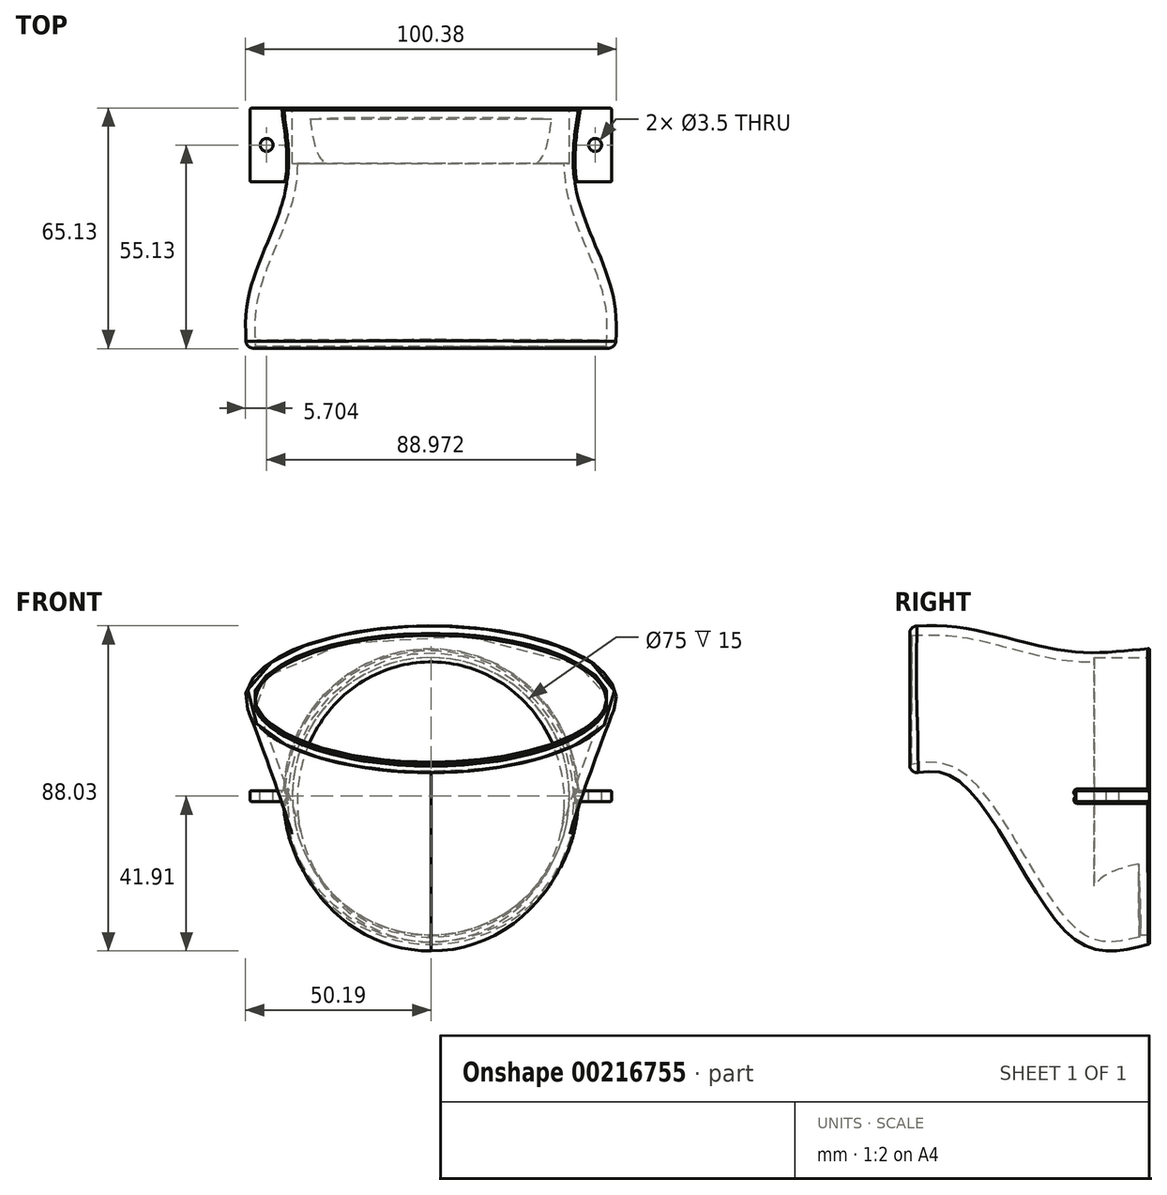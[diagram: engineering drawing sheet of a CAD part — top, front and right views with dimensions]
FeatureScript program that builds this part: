
annotation { "Feature Type Name" : "Feature", "Feature Type Description" : "" }
export const myFeature = defineFeature(function(context is Context, id is Id, definition is map)
    precondition{}
    {
        {
            var Q0;
            Q0=qCreatedBy(makeId("Front.planeOp"),FACE);
            var sketch = newSketch(context, id + "F0", { "sketchPlane" : qUnion([Q0])});
            skCircle(sketch, "E0", {"center": v(0, 0) * mm, "radius": 40 * mm});
            skSolve(sketch);
        }
        {
            var Q0;
            Q0=qCreatedBy(makeId("Front.planeOp"),FACE);
            cPlane(context, id + "F1", {"entities" : qUnion([Q0]), "cplaneType" : CPlaneType.OFFSET, "offset" : 20 * mm, "width" : 150 * mm, "height" : 150 * mm});
        }
        {
            var Q0;
            Q0=qCreatedBy(id+"F1.planeOp",FACE);
            var sketch = newSketch(context, id + "F2", { "sketchPlane" : qUnion([Q0])});
            skCircle(sketch, "E1", {"center": v(0, 0) * mm, "radius": 39 * mm});
            skSolve(sketch);
        }
        {
            var Q0;
            Q0=qCreatedBy(id+"F1.planeOp",FACE);
            cPlane(context, id + "F3", {"entities" : qUnion([Q0]), "cplaneType" : CPlaneType.OFFSET, "offset" : 35 * mm, "width" : 150 * mm, "height" : 150 * mm});
        }
        {
            var Q0;
            Q0=qCreatedBy(id+"F3.planeOp",FACE);
            var sketch = newSketch(context, id + "F4", { "sketchPlane" : qUnion([Q0])});
            skEllipse(sketch, "E2", {"center": v(0, 26) * mm, "majorRadius": 50 * mm, "minorRadius": 20 * mm, "majorAxis": v(1, 0)});
            skSolve(sketch);
        }
        {
            var Q0;
            Q0=qCreatedBy(id+"F3.planeOp",FACE);
            cPlane(context, id + "F5", {"entities" : qUnion([Q0]), "cplaneType" : CPlaneType.OFFSET, "offset" : 10 * mm, "width" : 150 * mm, "height" : 150 * mm});
        }
        {
            var Q0;
            Q0=qCreatedBy(id+"F5.planeOp",FACE);
            var sketch = newSketch(context, id + "F6", { "sketchPlane" : qUnion([Q0])});
            skEllipse(sketch, "E3", {"center": v(0, 26) * mm, "majorRadius": 50 * mm, "minorRadius": 20 * mm, "majorAxis": v(1, 0)});
            skSolve(sketch);
        }
        {
            var Q0;
            Q0=makeQuery(id+"F0.imprint","IMPRINT",FACE,{"disambiguationData":[TD([[makeQuery(id+"F0.imprint","IMPRINT",EDGE,{"derivedFrom":sQuery(id+"F0.wireOp",EDGE,"E0")}),1.0]])]});
            var Q1;
            Q1=makeQuery(id+"F2.imprint","IMPRINT",FACE,{"disambiguationData":[TD([[makeQuery(id+"F2.imprint","IMPRINT",EDGE,{"derivedFrom":sQuery(id+"F2.wireOp",EDGE,"E1")}),1.0]])]});
            var Q2;
            Q2=makeQuery(id+"F4.imprint","IMPRINT",FACE,{"disambiguationData":[TD([[makeQuery(id+"F4.imprint","IMPRINT",EDGE,{"derivedFrom":sQuery(id+"F4.wireOp",EDGE,"E2")}),1.0]])]});
            var Q3;
            Q3=makeQuery(id+"F6.imprint","IMPRINT",FACE,{"disambiguationData":[TD([[makeQuery(id+"F6.imprint","IMPRINT",EDGE,{"derivedFrom":sQuery(id+"F6.wireOp",EDGE,"E3")}),1.0]])]});
            loft(context, id + "F7", {"sheetProfilesArray" : [{ "sheetProfileEntities" : qUnion([Q0]) }, { "sheetProfileEntities" : qUnion([Q1]) }, { "sheetProfileEntities" : qUnion([Q2]) }, { "sheetProfileEntities" : qUnion([Q3]) }]});
        }
        {
            var Q0;
            Q0=qCreatedBy(makeId("Right.planeOp"),FACE);
            cPlane(context, id + "F8", {"entities" : qUnion([Q0]), "cplaneType" : CPlaneType.OFFSET, "offset" : 49 * mm, "width" : 150 * mm, "height" : 150 * mm});
        }
        {
            var Q0;
            Q0=qCreatedBy(id+"F8.planeOp",FACE);
            var sketch = newSketch(context, id + "F9", { "sketchPlane" : qUnion([Q0])});
            skLineSegment(sketch, "E4.bottom", {"start": v(-20, 1.5) * mm, "end": v(0, 1.5) * mm});
            skLineSegment(sketch, "E4.top", {"start": v(-20, -1.5) * mm, "end": v(0, -1.5) * mm});
            skLineSegment(sketch, "E4.left", {"start": v(-20, 1.5) * mm, "end": v(-20, -1.5) * mm});
            skLineSegment(sketch, "E4.right", {"start": v(0, 1.5) * mm, "end": v(0, -1.5) * mm});
            skSolve(sketch);
        }
        {
            var Q0;
            Q0=makeQuery(id+"F7.opLoft","CAP_FACE",FACE,{"disambiguationData":[OSD([makeQuery(id+"F6.imprint","IMPRINT",FACE,{"disambiguationData":[TD([[makeQuery(id+"F6.imprint","IMPRINT",EDGE,{"derivedFrom":sQuery(id+"F6.wireOp",EDGE,"E3")}),1.0]])]})])],"isStart":true});
            var Q1;
            Q1=makeQuery(id+"F7.opLoft","SWEPT_BODY",BODY,{"disambiguationData":[OSD([makeQuery(id+"F0.imprint","IMPRINT",FACE,{"disambiguationData":[TD([[makeQuery(id+"F0.imprint","IMPRINT",EDGE,{"derivedFrom":sQuery(id+"F0.wireOp",EDGE,"E0")}),1.0]])]}),sQuery(id+"F2.wireOp",EDGE,"E1"),sQuery(id+"F4.wireOp",EDGE,"E2"),makeQuery(id+"F6.imprint","IMPRINT",FACE,{"disambiguationData":[TD([[makeQuery(id+"F6.imprint","IMPRINT",EDGE,{"derivedFrom":sQuery(id+"F6.wireOp",EDGE,"E3")}),1.0]])]})])]});
            shell(context, id + "F10", {"entities" : qUnion([Q0]), "parts" : qUnion([Q1]), "thickness" : 2.5 * mm});
        }
        {
            var Q0;
            Q0=makeQuery(id+"F7.opLoft","CAP_FACE",FACE,{"disambiguationData":[OSD([makeQuery(id+"F0.imprint","IMPRINT",FACE,{"disambiguationData":[TD([[makeQuery(id+"F0.imprint","IMPRINT",EDGE,{"derivedFrom":sQuery(id+"F0.wireOp",EDGE,"E0")}),1.0]])]})])],"isStart":true});
            var sketch = newSketch(context, id + "F11", { "sketchPlane" : qUnion([Q0])});
            skCircle(sketch, "E5", {"center": v(0, 0) * mm, "radius": 37.5 * mm});
            skSolve(sketch);
        }
        {
            var Q0;
            Q0 = qSketchRegion(id + "F11", true);
            extrude(context, id + "F12", {"entities" : qUnion([Q0]), "operationType" : NewBodyOperationType.REMOVE, "oppositeDirection" : true, "depth" : 15 * mm});
        }
        {
            var Q0;
            Q0 = qSketchRegion(id + "F9", true);
            extrude(context, id + "F13", {"entities" : qUnion([Q0]), "operationType" : NewBodyOperationType.ADD, "oppositeDirection" : true, "depth" : 11 * mm});
        }
        {
            var Q0;
            Q0=qCreatedBy(makeId("Right.planeOp"),FACE);
            cPlane(context, id + "F14", {"entities" : qUnion([Q0]), "cplaneType" : CPlaneType.OFFSET, "offset" : 49 * mm, "oppositeDirection" : true, "width" : 150 * mm, "height" : 150 * mm});
        }
        {
            var Q0;
            Q0=qCreatedBy(id+"F14.planeOp",FACE);
            var sketch = newSketch(context, id + "F15", { "sketchPlane" : qUnion([Q0])});
            skLineSegment(sketch, "E6.bottom", {"start": v(0, 1.5) * mm, "end": v(-20, 1.5) * mm});
            skLineSegment(sketch, "E6.top", {"start": v(0, -1.5) * mm, "end": v(-20, -1.5) * mm});
            skLineSegment(sketch, "E6.left", {"start": v(0, 1.5) * mm, "end": v(0, -1.5) * mm});
            skLineSegment(sketch, "E6.right", {"start": v(-20, 1.5) * mm, "end": v(-20, -1.5) * mm});
            skSolve(sketch);
        }
        {
            var Q0;
            Q0 = qSketchRegion(id + "F15", true);
            var Q1;
            Q1 = qSketchRegion(id + "F17", true);
            extrude(context, id + "F16", {"entities" : qUnion([Q0, Q1]), "operationType" : NewBodyOperationType.ADD, "depth" : 11 * mm});
        }
        {
            var Q0;
            Q0=makeQuery(id+"F16.opExtrude","SWEPT_FACE",FACE,{"disambiguationData":[OSD([sQuery(id+"F15.wireOp",EDGE,"E6.bottom")])]});
            var sketch = newSketch(context, id + "F17", { "sketchPlane" : qUnion([Q0])});
            skCircle(sketch, "E7", {"center": v(-44.49, -10) * mm, "radius": 1.75 * mm});
            skPoint(sketch, "E7.centerSnap0", {"position": v(-44.49, 0) * mm});
            skCircle(sketch, "E8.MirrorC", {"center": v(44.49, -10) * mm, "radius": 1.75 * mm});
            skSolve(sketch);
        }
        {
            var Q0;
            Q0 = qSketchRegion(id + "F17", true);
            extrude(context, id + "F18", {"entities" : qUnion([Q0]), "operationType" : NewBodyOperationType.REMOVE, "endBound" : BoundingType.THROUGH_ALL, "oppositeDirection" : true, "depth" : 25 * mm});
        }
        {
            var Q0;
            Q0=makeQuery(id+"F12.boolean.opBoolean","COPY",EDGE,{"derivedFrom":makeQuery(id+"F12.opExtrude","CAP_EDGE",EDGE,{"disambiguationData":[OSD([sQuery(id+"F11.wireOp",EDGE,"E5")])],"isStart":true})});
            var Q1;
            Q1=makeQuery(id+"F10.opShell","OFFSET_EDGE",EDGE,{"disambiguationData":[OSD([sQuery(id+"F0.wireOp",EDGE,"E0"),sQuery(id+"F6.wireOp",EDGE,"E3")])]});
            chamfer(context, id + "F19", {"entities" : qUnion([Q0, Q1]), "width" : .5 * mm, "tangentPropagation" : true});
        }
        {
            var Q0;
            Q0=makeQuery(id+"F7.opLoft","MID_CAP_EDGE",EDGE,{"disambiguationData":[OSD([sQuery(id+"F0.wireOp",EDGE,"E0"),sQuery(id+"F6.wireOp",EDGE,"E3")])],"capPos":3.0});
            fillet(context, id + "F20", {"entities" : qUnion([Q0]), "radius" : 2 * mm, "tangentPropagation" : true, "allowEdgeOverflow" : false});
        }
        {
            var Q0;
            Q0=makeQuery(id+"F13.boolean.opBoolean","INTERSECT",EDGE,{"derivedFrom":[makeQuery(id+"F7.opLoft","SWEPT_FACE",FACE,{"disambiguationData":[OSD([sQuery(id+"F0.wireOp",EDGE,"E0"),sQuery(id+"F2.wireOp",EDGE,"E1")])]}),makeQuery(id+"F13.opExtrude","SWEPT_FACE",FACE,{"disambiguationData":[OSD([sQuery(id+"F9.wireOp",EDGE,"E4.bottom")])]})]});
            var Q1;
            Q1=makeQuery(id+"F13.boolean.opBoolean","INTERSECT",EDGE,{"derivedFrom":[makeQuery(id+"F7.opLoft","SWEPT_FACE",FACE,{"disambiguationData":[OSD([sQuery(id+"F0.wireOp",EDGE,"E0"),sQuery(id+"F2.wireOp",EDGE,"E1")])]}),makeQuery(id+"F13.opExtrude","SWEPT_FACE",FACE,{"disambiguationData":[OSD([sQuery(id+"F9.wireOp",EDGE,"E4.top")])]})]});
            var Q2;
            {var subQ0=sQuery(id+"F0.wireOp",EDGE,"E0");Q2=makeQuery(id+"F16.boolean.opBoolean","SPLIT",EDGE,{"disambiguationData":[TD([makeQuery(id+"F13.opExtrude","SWEPT_FACE",FACE,{"disambiguationData":[OSD([sQuery(id+"F9.wireOp",EDGE,"E4.bottom")])]})])],"derivedFrom":makeQuery(id+"F7.opLoft","MID_CAP_EDGE",EDGE,{"disambiguationData":[OSD([subQ0])],"capPos":0.0})});}
            var Q3;
            {var subQ0=sQuery(id+"F0.wireOp",EDGE,"E0");Q3=makeQuery(id+"F16.boolean.opBoolean","SPLIT",EDGE,{"disambiguationData":[TD([makeQuery(id+"F13.opExtrude","SWEPT_FACE",FACE,{"disambiguationData":[OSD([sQuery(id+"F9.wireOp",EDGE,"E4.top")])]})])],"derivedFrom":makeQuery(id+"F7.opLoft","MID_CAP_EDGE",EDGE,{"disambiguationData":[OSD([subQ0])],"capPos":0.0})});}
            var Q4;
            Q4=makeQuery(id+"F16.opExtrude","SWEPT_EDGE",EDGE,{"disambiguationData":[OSD([sQuery(id+"F15.wireOp",EDGE,"E6.bottom"),sQuery(id+"F15.wireOp",EDGE,"E6.left")])]});
            var Q5;
            Q5=makeQuery(id+"F16.opExtrude","SWEPT_EDGE",EDGE,{"disambiguationData":[OSD([sQuery(id+"F15.wireOp",EDGE,"E6.top"),sQuery(id+"F15.wireOp",EDGE,"E6.left")])]});
            var Q6;
            Q6=makeQuery(id+"F16.boolean.opBoolean","INTERSECT",EDGE,{"derivedFrom":[makeQuery(id+"F7.opLoft","SWEPT_FACE",FACE,{"disambiguationData":[OSD([sQuery(id+"F0.wireOp",EDGE,"E0"),sQuery(id+"F2.wireOp",EDGE,"E1")])]}),makeQuery(id+"F16.opExtrude","SWEPT_FACE",FACE,{"disambiguationData":[OSD([sQuery(id+"F15.wireOp",EDGE,"E6.bottom")])]})]});
            var Q7;
            Q7=makeQuery(id+"F16.boolean.opBoolean","INTERSECT",EDGE,{"derivedFrom":[makeQuery(id+"F7.opLoft","SWEPT_FACE",FACE,{"disambiguationData":[OSD([sQuery(id+"F0.wireOp",EDGE,"E0"),sQuery(id+"F2.wireOp",EDGE,"E1")])]}),makeQuery(id+"F16.opExtrude","SWEPT_FACE",FACE,{"disambiguationData":[OSD([sQuery(id+"F15.wireOp",EDGE,"E6.top")])]})]});
            var Q8;
            Q8=makeQuery(id+"F16.opExtrude","SWEPT_EDGE",EDGE,{"disambiguationData":[OSD([sQuery(id+"F15.wireOp",EDGE,"E6.bottom"),sQuery(id+"F15.wireOp",EDGE,"E6.right")])]});
            var Q9;
            Q9=makeQuery(id+"F16.opExtrude","SWEPT_EDGE",EDGE,{"disambiguationData":[OSD([sQuery(id+"F15.wireOp",EDGE,"E6.top"),sQuery(id+"F15.wireOp",EDGE,"E6.right")])]});
            var Q10;
            Q10=makeQuery(id+"F16.opExtrude","CAP_EDGE",EDGE,{"disambiguationData":[OSD([sQuery(id+"F15.wireOp",EDGE,"E6.right")])],"isStart":true});
            var Q11;
            Q11=makeQuery(id+"F16.opExtrude","CAP_EDGE",EDGE,{"disambiguationData":[OSD([sQuery(id+"F15.wireOp",EDGE,"E6.top")])],"isStart":true});
            var Q12;
            Q12=makeQuery(id+"F16.opExtrude","CAP_EDGE",EDGE,{"disambiguationData":[OSD([sQuery(id+"F15.wireOp",EDGE,"E6.bottom")])],"isStart":true});
            var Q13;
            Q13=makeQuery(id+"F16.opExtrude","CAP_EDGE",EDGE,{"disambiguationData":[OSD([sQuery(id+"F15.wireOp",EDGE,"E6.left")])],"isStart":true});
            var Q14;
            Q14=makeQuery(id+"F13.opExtrude","CAP_EDGE",EDGE,{"disambiguationData":[OSD([sQuery(id+"F9.wireOp",EDGE,"E4.bottom")])],"isStart":true});
            var Q15;
            Q15=makeQuery(id+"F13.opExtrude","CAP_EDGE",EDGE,{"disambiguationData":[OSD([sQuery(id+"F9.wireOp",EDGE,"E4.top")])],"isStart":true});
            var Q16;
            Q16=makeQuery(id+"F13.opExtrude","CAP_EDGE",EDGE,{"disambiguationData":[OSD([sQuery(id+"F9.wireOp",EDGE,"E4.right")])],"isStart":true});
            var Q17;
            Q17=makeQuery(id+"F13.opExtrude","SWEPT_EDGE",EDGE,{"disambiguationData":[OSD([sQuery(id+"F9.wireOp",EDGE,"E4.bottom"),sQuery(id+"F9.wireOp",EDGE,"E4.left")])]});
            var Q18;
            Q18=makeQuery(id+"F13.opExtrude","CAP_EDGE",EDGE,{"disambiguationData":[OSD([sQuery(id+"F9.wireOp",EDGE,"E4.left")])],"isStart":true});
            var Q19;
            Q19=makeQuery(id+"F13.opExtrude","SWEPT_EDGE",EDGE,{"disambiguationData":[OSD([sQuery(id+"F9.wireOp",EDGE,"E4.top"),sQuery(id+"F9.wireOp",EDGE,"E4.left")])]});
            fillet(context, id + "F21", {"entities" : qUnion([Q0, Q1, Q2, Q3, Q4, Q5, Q6, Q7, Q8, Q9, Q10, Q11, Q12, Q13, Q14, Q15, Q16, Q17, Q18, Q19]), "radius" : .5 * mm, "tangentPropagation" : true, "allowEdgeOverflow" : false});
        }
    });
